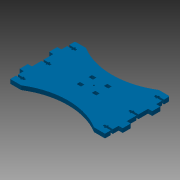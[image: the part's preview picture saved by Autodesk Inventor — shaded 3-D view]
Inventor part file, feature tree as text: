
AUTODESK INVENTOR PART (.ipt)
format: ipt  version: 2013 (Build 170138000, 138)  size: 279,040 bytes
history: native  units: mm
features: extrude x2, sketch x2
ambient origin geometry x8: Origin, YZ Plane, XZ Plane, XY Plane, X Axis, Y Axis, Z Axis, Center Point
bodies: Solid1 (feature_tree)
feature tree (4):
  extrude  "Extrusion1"  Depth=2.0mm
  extrude  "Extrusion2"  Depth=6.6mm
  sketch  "Sketch1"  dims[d0=58.936344mm d1=139.000017mm d2=95.0mm d3=55.807226mm d4=6.0mm d5=2.0mm d6=12.0mm d7=12.0mm d8=11.73562mm d9=2.93562mm d10=1.8mm d11=3.0mm d12=1.25mm d13=1.25mm d14=8.5mm d15=3.0mm d16=1.25mm d17=1.25mm d18=8.5mm d19=19.9mm d20=0.1mm d21=11.8mm d22=46.0mm d23=3.0mm d24=1.25mm d25=1.25mm d26=19.9mm d27=6.4mm d28=5.0mm d29=6.4mm d30=5.0mm d31=12.6mm d32=16.0mm d33=30.099983mm d34=55.100017mm d35=11.803343mm d36=3.0mm d37=1.799994mm d38=6.0mm d39=12.0mm d40=10.0mm d41=63.5mm d43=2.0mm]
  sketch  "Sketch2"  dims[d44=8.000008mm d45=6.6mm d46=6.0mm d47=0.0mm d48=10.0mm d49=0.0mm d50=47.5mm d51=203.186579mm d52=86.453462mm]
